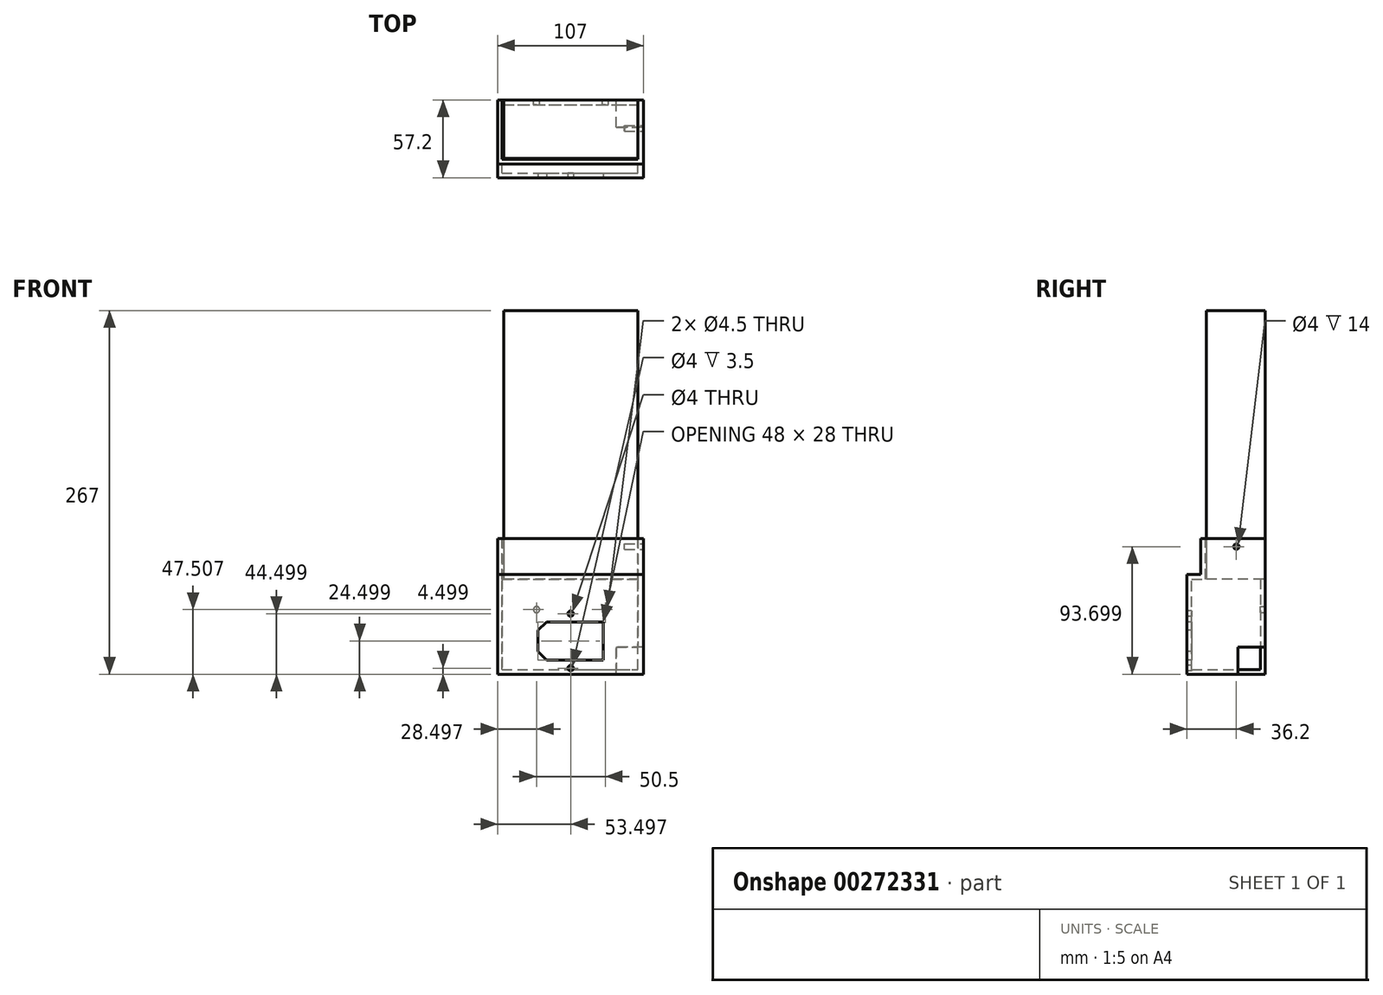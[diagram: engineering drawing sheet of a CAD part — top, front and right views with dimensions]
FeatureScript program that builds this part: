
annotation { "Feature Type Name" : "Feature", "Feature Type Description" : "" }
export const myFeature = defineFeature(function(context is Context, id is Id, definition is map)
    precondition{}
    {
        {
            var Q0;
            Q0=qCreatedBy(makeId("Front.planeOp"),FACE);
            var sketch = newSketch(context, id + "F0", { "sketchPlane" : qUnion([Q0])});
            skLineSegment(sketch, "E0.bottom", {"start": v(-59.6, 126.13) * mm, "end": v(38.9, 126.13) * mm});
            skLineSegment(sketch, "E0.top", {"start": v(-59.6, -70.87) * mm, "end": v(38.9, -70.87) * mm});
            skLineSegment(sketch, "E0.left", {"start": v(-59.6, 126.13) * mm, "end": v(-59.6, -70.87) * mm});
            skLineSegment(sketch, "E0.right", {"start": v(38.9, 126.13) * mm, "end": v(38.9, -70.87) * mm});
            skSolve(sketch);
        }
        {
            var Q0;
            Q0=makeQuery(id+"F0.imprint","IMPRINT",FACE,{"disambiguationData":[TD([[makeQuery(id+"F0.imprint","IMPRINT",EDGE,{"derivedFrom":sQuery(id+"F0.wireOp",EDGE,"E0.bottom")}),-1.0]])]});
            extrude(context, id + "F1", {"entities" : qUnion([Q0]), "depth" : 43 * mm});
        }
        {
            var Q0;
            Q0=makeQuery(id+"F1.opExtrude","SWEPT_FACE",FACE,{"disambiguationData":[OSD([sQuery(id+"F0.wireOp",EDGE,"E0.right")])]});
            var sketch = newSketch(context, id + "F2", { "sketchPlane" : qUnion([Q0])});
            skCircle(sketch, "E1", {"center": v(-21, -47.17) * mm, "radius": 2 * mm});
            skSolve(sketch);
        }
        {
            var Q0;
            Q0=makeQuery(id+"F2.imprint","IMPRINT",FACE,{"disambiguationData":[TD([[makeQuery(id+"F2.imprint","IMPRINT",EDGE,{"derivedFrom":sQuery(id+"F2.wireOp",EDGE,"JZKWuPf6-PGso-EqNF-yNsx-eXrz9TnsRI6m")}),1.0]])]});
            var Q1;
            Q1=makeQuery(id+"F2.imprint","IMPRINT",FACE,{"disambiguationData":[TD([[makeQuery(id+"F2.imprint","IMPRINT",EDGE,{"derivedFrom":sQuery(id+"F2.wireOp",EDGE,"E1")}),1.0]])]});
            extrude(context, id + "F3", {"entities" : qUnion([Q0, Q1]), "operationType" : NewBodyOperationType.REMOVE, "oppositeDirection" : true, "depth" : 10 * mm});
        }
        {
            var Q0;
            Q0=makeQuery(id+"F1.opExtrude","SWEPT_FACE",FACE,{"disambiguationData":[OSD([sQuery(id+"F0.wireOp",EDGE,"E0.right")])]});
            var sketch = newSketch(context, id + "F4", { "sketchPlane" : qUnion([Q0])});
            skLineSegment(sketch, "E2.bottom", {"start": v(-47.2, -41.17) * mm, "end": v(0, -41.17) * mm});
            skLineSegment(sketch, "E2.top", {"start": v(-47.2, -140.87) * mm, "end": v(0, -140.87) * mm});
            skLineSegment(sketch, "E2.left", {"start": v(-47.2, -67.5) * mm, "end": v(-47.2, -41.17) * mm});
            skLineSegment(sketch, "E2.right", {"start": v(0, -140.87) * mm, "end": v(0, -41.17) * mm});
            skLineSegment(sketch, "E3", {"start": v(-47.2, -140.87) * mm, "end": v(-57.2, -140.87) * mm});
            skLineSegment(sketch, "E4", {"start": v(-57.2, -140.87) * mm, "end": v(-57.2, -67.5) * mm});
            skLineSegment(sketch, "E5", {"start": v(-57.2, -67.5) * mm, "end": v(-47.2, -67.5) * mm});
            skSolve(sketch);
        }
        {
            var Q0;
            {var subQ3=sQuery(id+"F4.wireOp",EDGE,"E2.bottom");Q0=makeQuery(id+"F4.imprint","IMPRINT",FACE,{"disambiguationData":[TD([[makeQuery(id+"F4.imprint","IMPRINT",EDGE,{"derivedFrom":subQ3}),-1.0]])]});}
            var Q1;
            {var subQ0=sQuery(id+"F4.wireOp",EDGE,"E2.top");Q1=makeQuery(id+"F4.imprint","IMPRINT",FACE,{"disambiguationData":[TD([[makeQuery(id+"F4.imprint","IMPRINT",EDGE,{"derivedFrom":subQ0}),1.0]])]});}
            extrude(context, id + "F5", {"entities" : qUnion([Q0, Q1]), "depth" : 4 * mm});
        }
        {
            var Q0;
            Q0=makeQuery(id+"F5.opExtrude","CAP_FACE",FACE,{"disambiguationData":[OSD([sQuery(id+"F2.wireOp",EDGE,"E1"),sQuery(id+"F4.wireOp",EDGE,"E2.bottom"),sQuery(id+"F4.wireOp",EDGE,"E2.top"),sQuery(id+"F4.wireOp",EDGE,"E2.left"),sQuery(id+"F4.wireOp",EDGE,"E2.right")])],"isStart":true});
            var sketch = newSketch(context, id + "F6", { "sketchPlane" : qUnion([Q0])});
            skLineSegment(sketch, "E6.0", {"start": v(43.7, -44.67) * mm, "end": v(3.5, -44.67) * mm});
            skLineSegment(sketch, "E6.1", {"start": v(53.7, -137.37) * mm, "end": v(3.5, -137.37) * mm});
            skLineSegment(sketch, "E6.2", {"start": v(53.7, -137.37) * mm, "end": v(53.7, -71) * mm});
            skLineSegment(sketch, "E6.3", {"start": v(3.5, -44.67) * mm, "end": v(3.5, -137.37) * mm});
            skLineSegment(sketch, "E6.4", {"start": v(53.7, -71) * mm, "end": v(43.7, -71) * mm});
            skLineSegment(sketch, "E6.5", {"start": v(43.7, -71) * mm, "end": v(43.7, -44.67) * mm});
            skLineSegment(sketch, "E7", {"start": v(43.7, -44.67) * mm, "end": v(43.7, -41.17) * mm});
            skLineSegment(sketch, "E8", {"start": v(3.5, -70.87) * mm, "end": v(0, -70.87) * mm});
            skLineSegment(sketch, "E9", {"start": v(0, -70.87) * mm, "end": v(0, -140.87) * mm});
            skLineSegment(sketch, "E10", {"start": v(0, -140.87) * mm, "end": v(57.2, -140.87) * mm});
            skLineSegment(sketch, "E11", {"start": v(57.2, -140.87) * mm, "end": v(57.2, -67.5) * mm});
            skLineSegment(sketch, "E12", {"start": v(57.2, -67.5) * mm, "end": v(47.2, -67.5) * mm});
            skLineSegment(sketch, "E13", {"start": v(47.2, -67.5) * mm, "end": v(47.2, -41.17) * mm});
            skLineSegment(sketch, "E14", {"start": v(47.2, -41.17) * mm, "end": v(43.7, -41.17) * mm});
            skSolve(sketch);
        }
        {
            var Q0;
            {var subQ1=sQuery(id+"F6.wireOp",EDGE,"E6.1");Q0=makeQuery(id+"F6.imprint","IMPRINT",FACE,{"disambiguationData":[TD([[makeQuery(id+"F6.imprint","IMPRINT",EDGE,{"derivedFrom":subQ1}),1.0]])]});}
            extrude(context, id + "F7", {"entities" : qUnion([Q0]), "operationType" : NewBodyOperationType.ADD, "depth" : 100 * mm});
        }
        {
            var Q0;
            Q0=makeQuery(id+"F7.opExtrude","CAP_FACE",FACE,{"disambiguationData":[OSD([sQuery(id+"F6.wireOp",EDGE,"E6.1"),sQuery(id+"F6.wireOp",EDGE,"E6.2"),sQuery(id+"F6.wireOp",EDGE,"E6.3"),sQuery(id+"F6.wireOp",EDGE,"E6.4"),sQuery(id+"F6.wireOp",EDGE,"E6.5"),sQuery(id+"F6.wireOp",EDGE,"E7"),sQuery(id+"F6.wireOp",EDGE,"E8"),sQuery(id+"F6.wireOp",EDGE,"E9"),sQuery(id+"F6.wireOp",EDGE,"E10"),sQuery(id+"F6.wireOp",EDGE,"E11"),sQuery(id+"F6.wireOp",EDGE,"E12"),sQuery(id+"F6.wireOp",EDGE,"E13"),sQuery(id+"F6.wireOp",EDGE,"E14")])],"isStart":false});
            var sketch = newSketch(context, id + "F8", { "sketchPlane" : qUnion([Q0])});
            skLineSegment(sketch, "E15", {"start": v(0, -140.87) * mm, "end": v(57.2, -140.87) * mm});
            skLineSegment(sketch, "E16", {"start": v(57.2, -140.87) * mm, "end": v(57.2, -67.5) * mm});
            skLineSegment(sketch, "E17", {"start": v(57.2, -67.5) * mm, "end": v(47.2, -67.5) * mm});
            skLineSegment(sketch, "E18", {"start": v(47.2, -67.5) * mm, "end": v(47.2, -41.17) * mm});
            skLineSegment(sketch, "E19", {"start": v(47.2, -41.17) * mm, "end": v(43.7, -41.17) * mm});
            skLineSegment(sketch, "E20", {"start": v(43.7, -41.17) * mm, "end": v(0, -41.17) * mm});
            skLineSegment(sketch, "E21", {"start": v(0, -41.17) * mm, "end": v(0, -140.87) * mm});
            skSolve(sketch);
        }
        {
            var Q0;
            Q0=qSketchRegion(id+"F8",true);
            extrude(context, id + "F9", {"entities" : qUnion([Q0]), "operationType" : NewBodyOperationType.ADD, "depth" : 3 * mm});
        }
        {
            var Q0;
            Q0=makeQuery(id+"F9.boolean.opBoolean","MERGE",FACE,{"derivedFrom":[makeQuery(id+"F7.boolean.opBoolean","MERGE",FACE,{"derivedFrom":[makeQuery(id+"F5.opExtrude","SWEPT_FACE",FACE,{"disambiguationData":[OSD([sQuery(id+"F4.wireOp",EDGE,"E2.right")])]}),makeQuery(id+"F7.opExtrude","SWEPT_FACE",FACE,{"disambiguationData":[OSD([sQuery(id+"F6.wireOp",EDGE,"E9")])]})]}),makeQuery(id+"F9.opExtrude","SWEPT_FACE",FACE,{"disambiguationData":[OSD([sQuery(id+"F8.wireOp",EDGE,"E21")])]})]});
            var sketch = newSketch(context, id + "F10", { "sketchPlane" : qUnion([Q0])});
            skCircle(sketch, "E22", {"center": v(-14.9, -93.36) * mm, "radius": 2.25 * mm});
            skCircle(sketch, "E23", {"center": v(35.6, -93.36) * mm, "radius": 2.25 * mm});
            skLineSegment(sketch, "E24", {"start": v(-14.9, -93.36) * mm, "end": v(35.6, -93.36) * mm});
            skPoint(sketch, "E25", {"position": v(10.34, -93.36) * mm});
            skLineSegment(sketch, "E26", {"start": v(10.34, -93.36) * mm, "end": v(10.34, -70.87) * mm, "construction": true});
            skSolve(sketch);
        }
        {
            var Q0;
            Q0=makeQuery(id+"F10.imprint","IMPRINT",FACE,{"disambiguationData":[TD([[makeQuery(id+"F10.imprint","IMPRINT",EDGE,{"derivedFrom":sQuery(id+"F10.wireOp",EDGE,"E22")}),1.0]])]});
            var Q1;
            Q1=makeQuery(id+"F10.imprint","IMPRINT",FACE,{"disambiguationData":[TD([[makeQuery(id+"F10.imprint","IMPRINT",EDGE,{"derivedFrom":sQuery(id+"F10.wireOp",EDGE,"E23")}),1.0]])]});
            var Q2;
            Q2=makeQuery(id+"F7.opExtrude","SWEPT_FACE",FACE,{"disambiguationData":[OSD([sQuery(id+"F6.wireOp",EDGE,"E6.3")])]});
            extrude(context, id + "F11", {"entities" : qUnion([Q0, Q1]), "operationType" : NewBodyOperationType.REMOVE, "endBound" : BoundingType.UP_TO_SURFACE, "oppositeDirection" : true, "endBoundEntityFace" : qUnion([Q2]), "depth" : 25 * mm});
        }
        {
            var Q0;
            Q0=makeQuery(id+"F9.boolean.opBoolean","MERGE",FACE,{"derivedFrom":[makeQuery(id+"F7.boolean.opBoolean","MERGE",FACE,{"derivedFrom":[makeQuery(id+"F5.opExtrude","SWEPT_FACE",FACE,{"disambiguationData":[OSD([sQuery(id+"F4.wireOp",EDGE,"E4")])]}),makeQuery(id+"F7.opExtrude","SWEPT_FACE",FACE,{"disambiguationData":[OSD([sQuery(id+"F6.wireOp",EDGE,"E11")])]})]}),makeQuery(id+"F9.opExtrude","SWEPT_FACE",FACE,{"disambiguationData":[OSD([sQuery(id+"F8.wireOp",EDGE,"E16")])]})]});
            var sketch = newSketch(context, id + "F12", { "sketchPlane" : qUnion([Q0])});
            skLineSegment(sketch, "E27", {"start": v(-10.6, -91.87) * mm, "end": v(-10.6, -140.87) * mm, "construction": true});
            skLineSegment(sketch, "E28", {"start": v(-40.1, -103.37) * mm, "end": v(-40.1, -129.37) * mm});
            skLineSegment(sketch, "E29", {"start": v(18.9, -103.37) * mm, "end": v(18.9, -129.37) * mm});
            skLineSegment(sketch, "E30", {"start": v(-40.1, -103.37) * mm, "end": v(-10.6, -91.87) * mm});
            skLineSegment(sketch, "E31", {"start": v(-10.6, -91.87) * mm, "end": v(18.9, -103.37) * mm});
            skLineSegment(sketch, "E32", {"start": v(18.9, -129.37) * mm, "end": v(-10.6, -140.87) * mm});
            skLineSegment(sketch, "E33", {"start": v(-10.6, -140.87) * mm, "end": v(-40.1, -129.37) * mm});
            skLineSegment(sketch, "E34", {"start": v(-40.1, -116.37) * mm, "end": v(18.9, -116.37) * mm, "construction": true});
            skCircle(sketch, "E35", {"center": v(-10.6, -96.37) * mm, "radius": 2 * mm});
            skCircle(sketch, "E36", {"center": v(-10.6, -136.37) * mm, "radius": 2 * mm});
            skLineSegment(sketch, "E37", {"start": v(-10.6, -96.37) * mm, "end": v(-10.6, -136.37) * mm, "construction": true});
            skPoint(sketch, "E38", {"position": v(-10.6, -116.37) * mm});
            skLineSegment(sketch, "E39.bottom", {"start": v(-28.1, -102.87) * mm, "end": v(12.9, -102.87) * mm});
            skLineSegment(sketch, "E39.top", {"start": v(-28.1, -129.87) * mm, "end": v(12.9, -129.87) * mm});
            skLineSegment(sketch, "E39.right", {"start": v(12.9, -102.87) * mm, "end": v(12.9, -129.87) * mm});
            skLineSegment(sketch, "E40", {"start": v(-34.1, -108.87) * mm, "end": v(-34.1, -123.87) * mm});
            skLineSegment(sketch, "E41", {"start": v(-34.1, -123.87) * mm, "end": v(-28.1, -129.87) * mm});
            skLineSegment(sketch, "E42", {"start": v(-34.1, -108.87) * mm, "end": v(-28.1, -102.87) * mm});
            skLineSegment(sketch, "E43", {"start": v(12.9, -116.37) * mm, "end": v(-34.1, -116.37) * mm, "construction": true});
            skPoint(sketch, "E43.endSnap0", {"position": v(12.9, -116.37) * mm});
            skLineSegment(sketch, "E44", {"start": v(-28.1, -102.87) * mm, "end": v(-28.1, -129.87) * mm, "construction": true});
            skLineSegment(sketch, "E45.0", {"start": v(-34.6, -108.66) * mm, "end": v(-34.6, -124.08) * mm});
            skLineSegment(sketch, "E45.1", {"start": v(-28.3, -102.37) * mm, "end": v(13.4, -102.37) * mm});
            skLineSegment(sketch, "E45.2", {"start": v(13.4, -102.37) * mm, "end": v(13.4, -130.37) * mm});
            skLineSegment(sketch, "E45.3", {"start": v(-34.6, -108.66) * mm, "end": v(-28.3, -102.37) * mm});
            skLineSegment(sketch, "E45.4", {"start": v(-28.3, -130.37) * mm, "end": v(13.4, -130.37) * mm});
            skLineSegment(sketch, "E45.5", {"start": v(-34.6, -124.08) * mm, "end": v(-28.3, -130.37) * mm});
            skSolve(sketch);
        }
        {
            var Q0;
            Q0=makeQuery(id+"F12.imprint","IMPRINT",FACE,{"disambiguationData":[TD([[makeQuery(id+"F12.imprint","IMPRINT",EDGE,{"derivedFrom":sQuery(id+"F12.wireOp",EDGE,"E39.bottom")}),1.0]])]});
            var Q1;
            Q1=makeQuery(id+"F12.imprint","IMPRINT",FACE,{"disambiguationData":[TD([[makeQuery(id+"F12.imprint","IMPRINT",EDGE,{"derivedFrom":sQuery(id+"F12.wireOp",EDGE,"E39.bottom")}),-1.0]])]});
            var Q2;
            Q2=makeQuery(id+"F12.imprint","IMPRINT",FACE,{"disambiguationData":[TD([[makeQuery(id+"F12.imprint","IMPRINT",EDGE,{"derivedFrom":sQuery(id+"F12.wireOp",EDGE,"E36")}),1.0]])]});
            var Q3;
            Q3=makeQuery(id+"F12.imprint","IMPRINT",FACE,{"disambiguationData":[TD([[makeQuery(id+"F12.imprint","IMPRINT",EDGE,{"derivedFrom":sQuery(id+"F12.wireOp",EDGE,"E35")}),1.0]])]});
            var Q4;
            Q4=makeQuery(id+"F7.opExtrude","SWEPT_FACE",FACE,{"disambiguationData":[OSD([sQuery(id+"F6.wireOp",EDGE,"E6.2")])]});
            extrude(context, id + "F13", {"entities" : qUnion([Q0, Q1, Q2, Q3]), "operationType" : NewBodyOperationType.REMOVE, "endBound" : BoundingType.UP_TO_SURFACE, "oppositeDirection" : true, "endBoundEntityFace" : qUnion([Q4]), "depth" : 25 * mm});
        }
        {
            var Q0;
            Q0=makeQuery(id+"F9.boolean.opBoolean","MERGE",FACE,{"derivedFrom":[makeQuery(id+"F7.boolean.opBoolean","MERGE",FACE,{"derivedFrom":[makeQuery(id+"F5.opExtrude","SWEPT_FACE",FACE,{"disambiguationData":[OSD([sQuery(id+"F4.wireOp",EDGE,"E2.right")])]}),makeQuery(id+"F7.opExtrude","SWEPT_FACE",FACE,{"disambiguationData":[OSD([sQuery(id+"F6.wireOp",EDGE,"E9")])]})]}),makeQuery(id+"F9.opExtrude","SWEPT_FACE",FACE,{"disambiguationData":[OSD([sQuery(id+"F8.wireOp",EDGE,"E21")])]})]});
            var sketch = newSketch(context, id + "F14", { "sketchPlane" : qUnion([Q0])});
            skLineSegment(sketch, "E46.bottom", {"start": v(-42.9, -140.87) * mm, "end": v(-22.9, -140.87) * mm});
            skLineSegment(sketch, "E46.top", {"start": v(-42.9, -120.87) * mm, "end": v(-22.9, -120.87) * mm});
            skLineSegment(sketch, "E46.left", {"start": v(-42.9, -140.87) * mm, "end": v(-42.9, -120.87) * mm});
            skLineSegment(sketch, "E46.right", {"start": v(-22.9, -140.87) * mm, "end": v(-22.9, -120.87) * mm});
            skSolve(sketch);
        }
        {
            var Q0;
            Q0=makeQuery(id+"F14.imprint","IMPRINT",FACE,{"disambiguationData":[TD([[makeQuery(id+"F14.imprint","IMPRINT",EDGE,{"derivedFrom":sQuery(id+"F14.wireOp",EDGE,"E46.bottom")}),1.0]])]});
            extrude(context, id + "F15", {"entities" : qUnion([Q0]), "operationType" : NewBodyOperationType.REMOVE, "oppositeDirection" : true, "depth" : 20 * mm});
        }
    });
